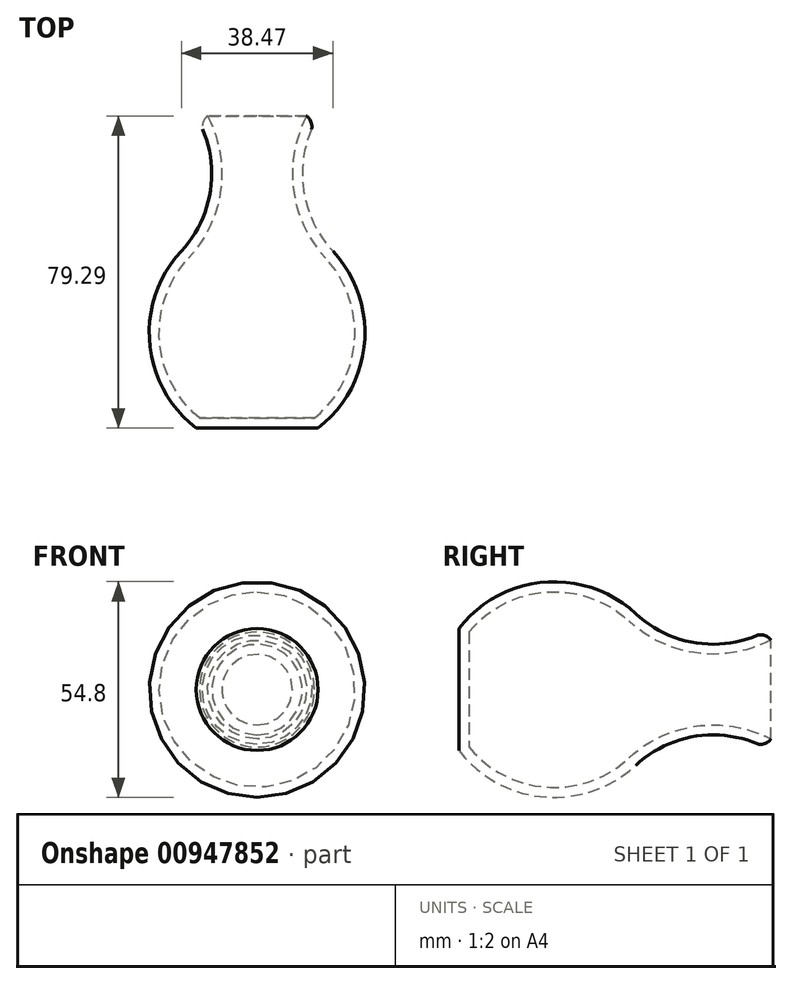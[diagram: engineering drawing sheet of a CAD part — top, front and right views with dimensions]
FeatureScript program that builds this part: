
annotation { "Feature Type Name" : "Feature", "Feature Type Description" : "" }
export const myFeature = defineFeature(function(context is Context, id is Id, definition is map)
    precondition{}
    {
        {
            var Q0;
            Q0=qCreatedBy(makeId("Top.planeOp"),FACE);
            var sketch = newSketch(context, id + "F0", { "sketchPlane" : qUnion([Q0])});
            skLineSegment(sketch, "E0", {"start": v(0, -53.22) * mm, "end": v(15.48, -53.22) * mm});
            skArc(sketch, "E1", {"start": v(-3.75, -8.22) * mm, "mid": v(-11.8, -31.55) * mm, "end": v(0, -53.22) * mm});
            skArc(sketch, "E2", {"start": v(-3.75, -8.22) * mm, "mid": v(3.8, 8.3) * mm, "end": v(0, 26.06) * mm});
            skLineSegment(sketch, "E3", {"start": v(15.48, -53.22) * mm, "end": v(15.48, 26.1) * mm});
            skLineSegment(sketch, "E4", {"start": v(0, 26.06) * mm, "end": v(15.48, 26.1) * mm});
            skSolve(sketch);
        }
        {
            var Q0;
            Q0=makeQuery(id+"F0.imprint","IMPRINT",FACE,{"disambiguationData":[TD([[makeQuery(id+"F0.imprint","IMPRINT",EDGE,{"derivedFrom":sQuery(id+"F0.wireOp",EDGE,"E0")}),1.0]])]});
            var Q1;
            Q1=sQuery(id+"F0.wireOp",EDGE,"E3");
            revolve(context, id + "F1", {"surfaceOperationType" : NewSurfaceOperationType.NEW, "entities" : qUnion([Q0]), "axis" : qUnion([Q1]), "revolveType" : RevolveType.FULL});
        }
        {
            var Q0;
            Q0=makeQuery(id+"F1.opRevolve","SWEPT_FACE",FACE,{"disambiguationData":[OSD([sQuery(id+"F0.wireOp",EDGE,"E4")])]});
            var Q1;
            Q1=makeQuery(id+"F1.opRevolve","SWEPT_BODY",BODY,{"disambiguationData":[OSD([sQuery(id+"F0.wireOp",EDGE,"E0"),sQuery(id+"F0.wireOp",EDGE,"E1"),sQuery(id+"F0.wireOp",EDGE,"E2"),sQuery(id+"F0.wireOp",EDGE,"E3"),sQuery(id+"F0.wireOp",EDGE,"E4")])]});
            shell(context, id + "F2", {"entities" : qUnion([Q0]), "parts" : qUnion([Q1]), "thickness" : 2.54 * mm});
        }
        {
            var Q0;
            Q0=makeQuery(id+"F1.opRevolve","SWEPT_EDGE",EDGE,{"disambiguationData":[OSD([sQuery(id+"F0.wireOp",EDGE,"E2"),sQuery(id+"F0.wireOp",EDGE,"E4")])]});
            fillet(context, id + "F3", {"entities" : qUnion([Q0]), "radius" : 2.54 * mm, "tangentPropagation" : true, "rho" : 0.3, "crossSection" : FilletCrossSection.CONIC, "allowEdgeOverflow" : false});
        }
    });
